# Revit family: RVT_MACOM_CBHS-DN-DG 03 23 A
name_source: partatom
category: Specialty Equipment
units: mm (PartAtom-declared; Revit-internal decimal feet)

## family parameters
Always vertical = Yes
Cut with Voids When Loaded = No
OmniClass Number = 23.40.40.14.17.21
OmniClass Title = Grills
Part Type = Normal
Room Calculation Point = No
Round Connector Dimension = Use Diameter
Shared = No
Work Plane-Based = No

## types (2) — shared parameters
Default Elevation = 0 mm
Gas Pressure GLP = 0,0 bar
Gas Pressure GN = 0,0 bar
Manufacturer = MACOM
URL = https://www.acosmacom.com.br
Volume = 0,31 m³

## per-type parameters (varying)
| type | Description | Gas Flow GLP | Gas Flow GN | Gas Input GLP | Gas Input GN |
| CBHS-DN | CHAR-BROILER MACOM HIGH POWER 406x819x911 mm |  | 1,1 m³/h | 0 Btu/h | 10528 Kcal/h |
| CBHS-DG | CHAR-BROILER MACOM HIGH POWER 406X819X911 mm | 0,93 Kg/h | 0,0 m³/h | 42490 Btu/h |  |

note: column(s) folded — value = type name in every type: Model

## geometry (parser evidence)
native form markers: Sweep x4
no freeform markers — native parametric forms only
